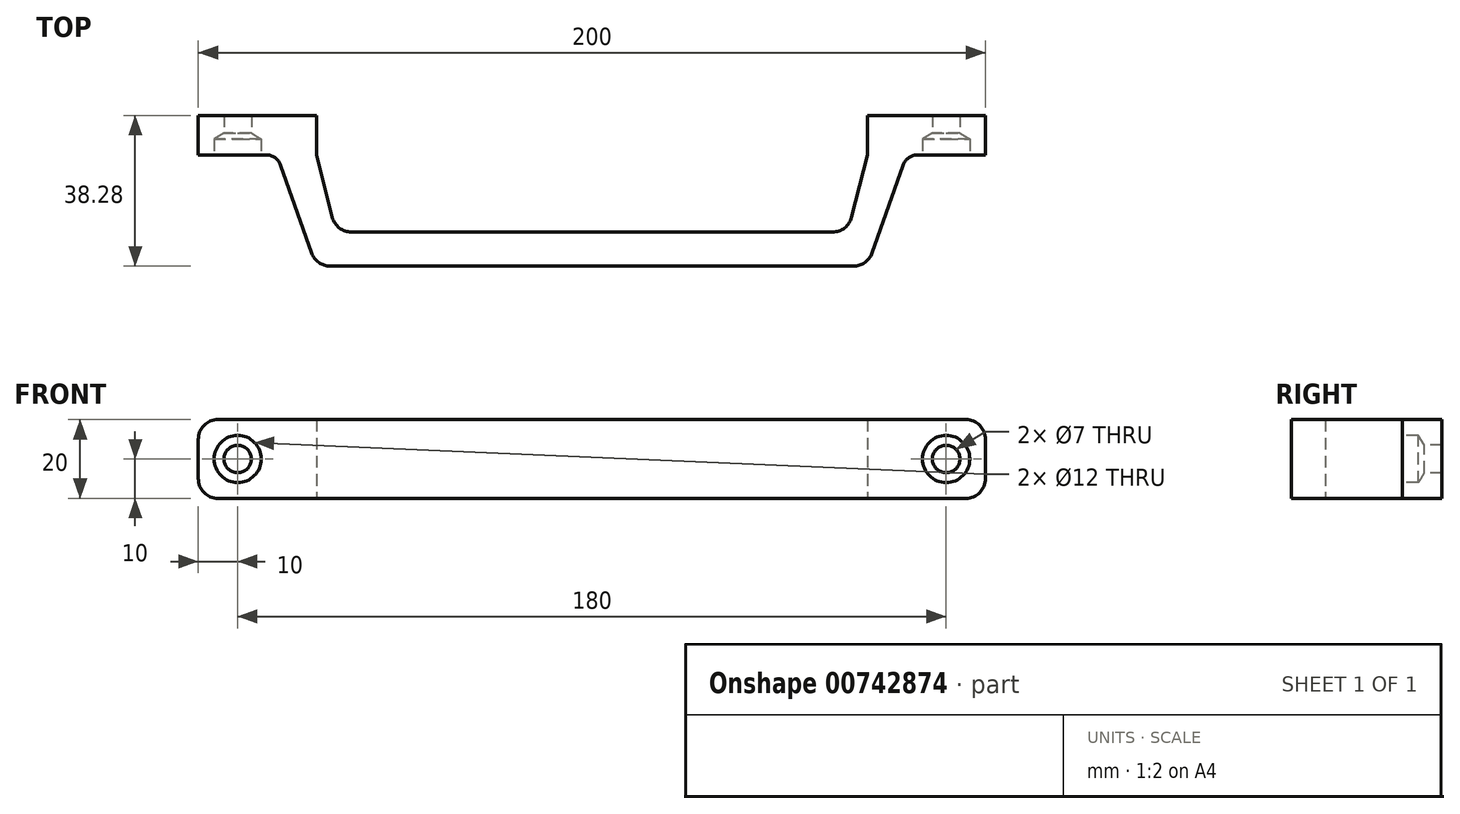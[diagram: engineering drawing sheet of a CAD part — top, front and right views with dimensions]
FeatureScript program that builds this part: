
annotation { "Feature Type Name" : "Feature", "Feature Type Description" : "" }
export const myFeature = defineFeature(function(context is Context, id is Id, definition is map)
    precondition{}
    {
        {
            var Q0;
            Q0=qCreatedBy(makeId("Top.planeOp"),FACE);
            var sketch = newSketch(context, id + "F0", { "sketchPlane" : qUnion([Q0])});
            skLineSegment(sketch, "E0.bottom", {"start": v(-100, 5) * mm, "end": v(100, 5) * mm});
            skLineSegment(sketch, "E0.top", {"start": v(-100, -5) * mm, "end": v(100, -5) * mm});
            skLineSegment(sketch, "E0.left", {"start": v(-100, 5) * mm, "end": v(-100, -5) * mm});
            skLineSegment(sketch, "E0.right", {"start": v(100, 5) * mm, "end": v(100, -5) * mm});
            skPoint(sketch, "E0.middle", {"position": v(0, 0) * mm});
            skLineSegment(sketch, "E1", {"start": v(-80, 5) * mm, "end": v(-80, -5) * mm});
            skLineSegment(sketch, "E2", {"start": v(80, -5) * mm, "end": v(80, 5) * mm});
            skLineSegment(sketch, "E3", {"start": v(-70, 5) * mm, "end": v(-70, -5) * mm});
            skLineSegment(sketch, "E4", {"start": v(70, 5) * mm, "end": v(70, -5) * mm});
            skLineSegment(sketch, "E5", {"start": v(-80, -5) * mm, "end": v(-70, -33.28) * mm});
            skLineSegment(sketch, "E6", {"start": v(-70, -33.28) * mm, "end": v(70, -33.28) * mm});
            skLineSegment(sketch, "E7", {"start": v(70, -33.28) * mm, "end": v(80, -5) * mm});
            skLineSegment(sketch, "E8", {"start": v(-70, -5) * mm, "end": v(-65, -24.62) * mm});
            skLineSegment(sketch, "E9", {"start": v(-65, -24.62) * mm, "end": v(65, -24.62) * mm});
            skLineSegment(sketch, "E10", {"start": v(65, -24.62) * mm, "end": v(70, -5) * mm});
            skSolve(sketch);
        }
        {
            var Q0;
            {var subQ0=sQuery(id+"F0.wireOp",EDGE,"E0.left");Q0=makeQuery(id+"F0.imprint","IMPRINT",FACE,{"disambiguationData":[TD([[makeQuery(id+"F0.imprint","IMPRINT",EDGE,{"derivedFrom":subQ0}),1.0]])]});}
            var Q1;
            {var subQ0=sQuery(id+"F0.wireOp",EDGE,"E5");Q1=makeQuery(id+"F0.imprint","IMPRINT",FACE,{"disambiguationData":[TD([[makeQuery(id+"F0.imprint","IMPRINT",EDGE,{"derivedFrom":subQ0}),1.0]])]});}
            var Q2;
            {var subQ0=sQuery(id+"F0.wireOp",EDGE,"E1");Q2=makeQuery(id+"F0.imprint","IMPRINT",FACE,{"disambiguationData":[TD([[makeQuery(id+"F0.imprint","IMPRINT",EDGE,{"derivedFrom":subQ0}),1.0]])]});}
            var Q3;
            {var subQ0=sQuery(id+"F0.wireOp",EDGE,"E2");Q3=makeQuery(id+"F0.imprint","IMPRINT",FACE,{"disambiguationData":[TD([[makeQuery(id+"F0.imprint","IMPRINT",EDGE,{"derivedFrom":subQ0}),1.0]])]});}
            var Q4;
            {var subQ0=sQuery(id+"F0.wireOp",EDGE,"E0.right");Q4=makeQuery(id+"F0.imprint","IMPRINT",FACE,{"disambiguationData":[TD([[makeQuery(id+"F0.imprint","IMPRINT",EDGE,{"derivedFrom":subQ0}),-1.0]])]});}
            extrude(context, id + "F1", {"entities" : qUnion([Q0, Q1, Q2, Q3, Q4]), "depth" : 20 * mm, "offsetDistance" : 25 * mm});
        }
        {
            var Q0;
            {var subQ0=sQuery(id+"F0.wireOp",EDGE,"E0.top");Q0=makeQuery(id+"F1.opExtrude","SWEPT_FACE",FACE,{"disambiguationData":[OSD([subQ0]),TDD([makeQuery(id+"F0.imprint","IMPRINT",EDGE,{"disambiguationData":[TD([[makeQuery(id+"F0.imprint","INTERSECT",VERTEX,{"derivedFrom":[subQ0,sQuery(id+"F0.wireOp",EDGE,"E0.left")]}),-1.0]])],"derivedFrom":subQ0})])]});}
            var sketch = newSketch(context, id + "F2", { "sketchPlane" : qUnion([Q0])});
            skCircle(sketch, "E11", {"center": v(-90, 10) * mm, "radius": 6 * mm});
            skPoint(sketch, "E11.centerSnap0", {"position": v(-90, 20) * mm});
            skCircle(sketch, "E12", {"center": v(90, 10) * mm, "radius": 6 * mm});
            skPoint(sketch, "E12.centerSnap0", {"position": v(-100, 10) * mm});
            skCircle(sketch, "E13", {"center": v(-90, 10) * mm, "radius": 3.5 * mm});
            skCircle(sketch, "E14", {"center": v(90, 10) * mm, "radius": 3.5 * mm});
            skSolve(sketch);
        }
        {
            var Q0;
            Q0=sQuery(id+"F2.wireOp",VERTEX,"E11.center");
            var Q1;
            Q1=sQuery(id+"F2.wireOp",VERTEX,"E12.center");
            var Q2;
            Q2=makeQuery(id+"F1.opExtrude","SWEPT_BODY",BODY,{"disambiguationData":[OSD([sQuery(id+"F0.wireOp",EDGE,"E0.bottom"),sQuery(id+"F0.wireOp",EDGE,"E0.top"),sQuery(id+"F0.wireOp",EDGE,"E0.left"),sQuery(id+"F0.wireOp",EDGE,"E0.right"),sQuery(id+"F0.wireOp",EDGE,"E3"),sQuery(id+"F0.wireOp",EDGE,"E4"),sQuery(id+"F0.wireOp",EDGE,"E5"),sQuery(id+"F0.wireOp",EDGE,"E6"),sQuery(id+"F0.wireOp",EDGE,"E7"),sQuery(id+"F0.wireOp",EDGE,"E8"),sQuery(id+"F0.wireOp",EDGE,"E9"),sQuery(id+"F0.wireOp",EDGE,"E10")])]});
            hole(context, id + "F3", {"style" : HoleStyle.SIMPLE, "endStyle" : HoleEndStyle.THROUGH, "holeDiameter" : 7 * mm, "majorDiameter" : 5 * mm, "isTappedThrough" : true, "tappedDepth" : 12 * mm, "tapClearance" : 3, "startFromSketch" : true, "locations" : qUnion([Q0, Q1]), "scope" : qUnion([Q2])});
        }
        {
            var Q0;
            Q0=sQuery(id+"F2.wireOp",VERTEX,"E11.center");
            var Q1;
            Q1=sQuery(id+"F2.wireOp",VERTEX,"E12.center");
            var Q2;
            Q2=makeQuery(id+"F1.opExtrude","SWEPT_BODY",BODY,{"disambiguationData":[OSD([sQuery(id+"F0.wireOp",EDGE,"E0.bottom"),sQuery(id+"F0.wireOp",EDGE,"E0.top"),sQuery(id+"F0.wireOp",EDGE,"E0.left"),sQuery(id+"F0.wireOp",EDGE,"E0.right"),sQuery(id+"F0.wireOp",EDGE,"E3"),sQuery(id+"F0.wireOp",EDGE,"E4"),sQuery(id+"F0.wireOp",EDGE,"E5"),sQuery(id+"F0.wireOp",EDGE,"E6"),sQuery(id+"F0.wireOp",EDGE,"E7"),sQuery(id+"F0.wireOp",EDGE,"E8"),sQuery(id+"F0.wireOp",EDGE,"E9"),sQuery(id+"F0.wireOp",EDGE,"E10")])]});
            hole(context, id + "F4", {"style" : HoleStyle.SIMPLE, "endStyle" : HoleEndStyle.BLIND, "holeDiameter" : 12 * mm, "majorDiameter" : 5 * mm, "holeDepth" : 4 * mm, "isTappedThrough" : true, "tappedDepth" : 12 * mm, "tapClearance" : 3, "startFromSketch" : true, "locations" : qUnion([Q0, Q1]), "scope" : qUnion([Q2])});
        }
        {
            var Q0;
            Q0=makeQuery(id+"F1.opExtrude","CAP_EDGE",EDGE,{"disambiguationData":[OSD([sQuery(id+"F0.wireOp",EDGE,"E0.left")])],"isStart":false});
            var Q1;
            Q1=makeQuery(id+"F1.opExtrude","CAP_EDGE",EDGE,{"disambiguationData":[OSD([sQuery(id+"F0.wireOp",EDGE,"E0.left")])],"isStart":true});
            var Q2;
            Q2=makeQuery(id+"F1.opExtrude","CAP_EDGE",EDGE,{"disambiguationData":[OSD([sQuery(id+"F0.wireOp",EDGE,"E0.right")])],"isStart":false});
            var Q3;
            Q3=makeQuery(id+"F1.opExtrude","CAP_EDGE",EDGE,{"disambiguationData":[OSD([sQuery(id+"F0.wireOp",EDGE,"E0.right")])],"isStart":true});
            fillet(context, id + "F5", {"entities" : qUnion([Q0, Q1, Q2, Q3]), "radius" : 5 * mm, "tangentPropagation" : true, "allowEdgeOverflow" : false});
        }
        {
            var Q0;
            Q0=makeQuery(id+"F1.opExtrude","SWEPT_EDGE",EDGE,{"disambiguationData":[OSD([sQuery(id+"F0.wireOp",EDGE,"E0.top"),sQuery(id+"F0.wireOp",EDGE,"E1"),sQuery(id+"F0.wireOp",EDGE,"E5")])]});
            var Q1;
            Q1=makeQuery(id+"F1.opExtrude","SWEPT_EDGE",EDGE,{"disambiguationData":[OSD([sQuery(id+"F0.wireOp",EDGE,"E0.top"),sQuery(id+"F0.wireOp",EDGE,"E2"),sQuery(id+"F0.wireOp",EDGE,"E7")])]});
            fillet(context, id + "F6", {"entities" : qUnion([Q0, Q1]), "radius" : 4 * mm, "tangentPropagation" : true, "allowEdgeOverflow" : false});
        }
        {
            var Q0;
            Q0=makeQuery(id+"F1.opExtrude","SWEPT_EDGE",EDGE,{"disambiguationData":[OSD([sQuery(id+"F0.wireOp",EDGE,"E5"),sQuery(id+"F0.wireOp",EDGE,"E6")])]});
            var Q1;
            Q1=makeQuery(id+"F1.opExtrude","SWEPT_EDGE",EDGE,{"disambiguationData":[OSD([sQuery(id+"F0.wireOp",EDGE,"E6"),sQuery(id+"F0.wireOp",EDGE,"E7")])]});
            var Q2;
            Q2=makeQuery(id+"F1.opExtrude","SWEPT_EDGE",EDGE,{"disambiguationData":[OSD([sQuery(id+"F0.wireOp",EDGE,"E8"),sQuery(id+"F0.wireOp",EDGE,"E9")])]});
            var Q3;
            Q3=makeQuery(id+"F1.opExtrude","SWEPT_EDGE",EDGE,{"disambiguationData":[OSD([sQuery(id+"F0.wireOp",EDGE,"E9"),sQuery(id+"F0.wireOp",EDGE,"E10")])]});
            fillet(context, id + "F7", {"entities" : qUnion([Q0, Q1, Q2, Q3]), "radius" : 5 * mm, "tangentPropagation" : true, "allowEdgeOverflow" : false});
        }
    });
